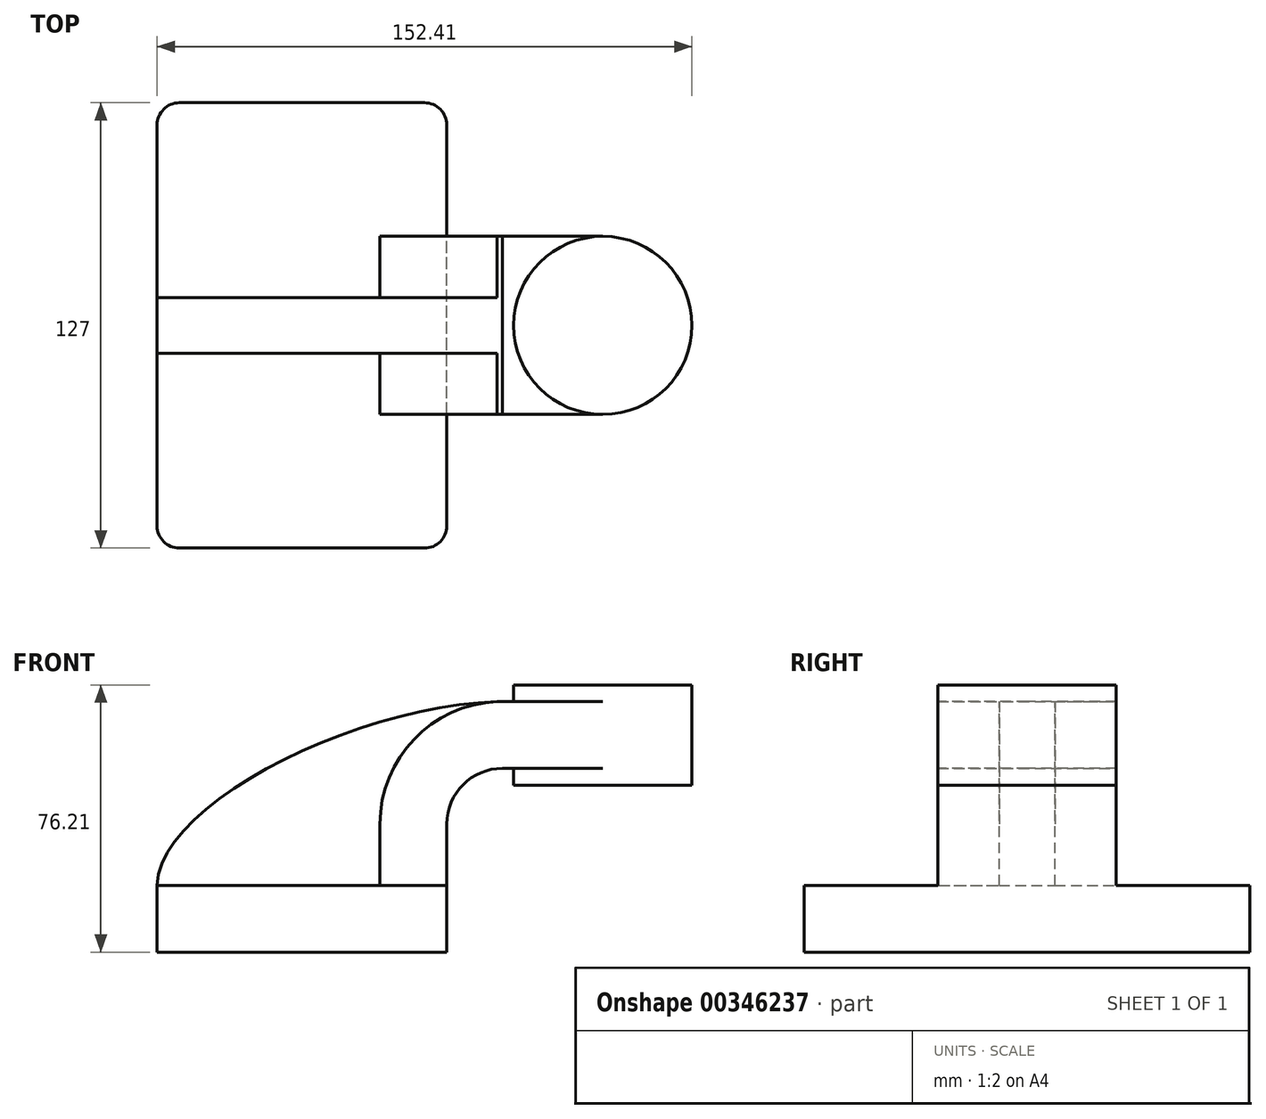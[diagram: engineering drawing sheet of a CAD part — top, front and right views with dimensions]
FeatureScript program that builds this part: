
annotation { "Feature Type Name" : "Feature", "Feature Type Description" : "" }
export const myFeature = defineFeature(function(context is Context, id is Id, definition is map)
    precondition{}
    {
        {
            var Q0;
            Q0=qCreatedBy(makeId("Front.planeOp"),FACE);
            var sketch = newSketch(context, id + "F0", { "sketchPlane" : qUnion([Q0])});
            skLineSegment(sketch, "E0.bottom", {"start": v(-41.28, -9.53) * mm, "end": v(41.28, -9.53) * mm});
            skLineSegment(sketch, "E0.top", {"start": v(-41.28, 9.52) * mm, "end": v(41.28, 9.52) * mm});
            skLineSegment(sketch, "E0.left", {"start": v(-41.28, -9.53) * mm, "end": v(-41.28, 9.52) * mm});
            skLineSegment(sketch, "E0.right", {"start": v(41.28, -9.53) * mm, "end": v(41.28, 9.52) * mm});
            skPoint(sketch, "E0.middle", {"position": v(0, 0) * mm});
            skLineSegment(sketch, "E1.bottom", {"start": v(60.32, 38.1) * mm, "end": v(111.12, 38.1) * mm});
            skLineSegment(sketch, "E1.top", {"start": v(60.32, 66.67) * mm, "end": v(111.12, 66.67) * mm});
            skLineSegment(sketch, "E1.left", {"start": v(60.32, 38.1) * mm, "end": v(60.32, 66.67) * mm});
            skLineSegment(sketch, "E1.right", {"start": v(111.12, 38.1) * mm, "end": v(111.12, 66.67) * mm});
            skPoint(sketch, "E1.middle", {"position": v(85.72, 52.39) * mm});
            skLineSegment(sketch, "E2", {"start": v(41.28, 9.52) * mm, "end": v(41.28, 27) * mm});
            skArc(sketch, "E3", {"start": v(41.27, 27) * mm, "mid": v(45.92, 38.23) * mm, "end": v(57.15, 42.88) * mm});
            skLineSegment(sketch, "E4", {"start": v(57.15, 42.88) * mm, "end": v(85.72, 42.88) * mm});
            skPoint(sketch, "E4.endSnap0", {"position": v(85.72, 38.1) * mm});
            skLineSegment(sketch, "E5.0", {"start": v(57.15, 61.93) * mm, "end": v(85.72, 61.93) * mm});
            skArc(sketch, "E5.1", {"start": v(22.23, 27) * mm, "mid": v(32.45, 51.7) * mm, "end": v(57.15, 61.93) * mm});
            skLineSegment(sketch, "E5.2", {"start": v(22.23, 9.52) * mm, "end": v(22.23, 27) * mm});
            skLineSegment(sketch, "E6", {"start": v(85.72, 38.1) * mm, "end": v(85.72, 66.67) * mm});
            skFitSpline(sketch, "E7", {"points": [v(-41.28, 9.52) * mm, v(57.15, 61.93) * mm], "startDerivative": vector(1.94, 71.16) * mm, "endDerivative": vector(121.36, 1.65) * mm});
            skSolve(sketch);
        }
        {
            var Q0;
            Q0=makeQuery(id+"F0.imprint","IMPRINT",FACE,{"disambiguationData":[TD([[makeQuery(id+"F0.imprint","IMPRINT",EDGE,{"derivedFrom":sQuery(id+"F0.wireOp",EDGE,"E0.bottom")}),1.0]])]});
            extrude(context, id + "F1", {"entities" : qUnion([Q0]), "endBound" : BoundingType.SYMMETRIC, "depth" : 127 * mm});
        }
        {
            var Q0;
            {var subQ1=sQuery(id+"F0.wireOp",EDGE,"E2");Q0=makeQuery(id+"F0.imprint","IMPRINT",FACE,{"disambiguationData":[TD([[makeQuery(id+"F0.imprint","IMPRINT",EDGE,{"derivedFrom":subQ1}),1.0]])]});}
            var Q1;
            {var subQ0=sQuery(id+"F0.wireOp",EDGE,"E4");var subQ1=sQuery(id+"F0.wireOp",EDGE,"E1.left");var subQ2=makeQuery(id+"F0.imprint","INTERSECT",VERTEX,{"derivedFrom":[subQ1,subQ0]});Q1=makeQuery(id+"F0.imprint","IMPRINT",FACE,{"disambiguationData":[TD([[makeQuery(id+"F0.imprint","IMPRINT",EDGE,{"disambiguationData":[TD([[subQ2,-1.0]])],"derivedFrom":subQ1}),-1.0]])]});}
            extrude(context, id + "F2", {"entities" : qUnion([Q0, Q1]), "operationType" : NewBodyOperationType.ADD, "endBound" : BoundingType.SYMMETRIC, "depth" : 50.8 * mm});
        }
        {
            var Q0;
            {var subQ3=sQuery(id+"F0.wireOp",EDGE,"E5.2");Q0=makeQuery(id+"F0.imprint","IMPRINT",FACE,{"disambiguationData":[TD([[makeQuery(id+"F0.imprint","IMPRINT",EDGE,{"derivedFrom":subQ3}),1.0]])]});}
            extrude(context, id + "F3", {"entities" : qUnion([Q0]), "operationType" : NewBodyOperationType.ADD, "endBound" : BoundingType.SYMMETRIC, "depth" : 15.88 * mm});
        }
        {
            var Q0;
            {var subQ4=sQuery(id+"F0.wireOp",EDGE,"E1.right");Q0=makeQuery(id+"F0.imprint","IMPRINT",FACE,{"disambiguationData":[TD([[makeQuery(id+"F0.imprint","IMPRINT",EDGE,{"derivedFrom":subQ4}),1.0]])]});}
            var Q1;
            Q1=sQuery(id+"F0.wireOp",EDGE,"E6");
            revolve(context, id + "F4", {"operationType" : NewBodyOperationType.ADD, "entities" : qUnion([Q0]), "axis" : qUnion([Q1]), "revolveType" : RevolveType.FULL});
        }
        {
            var Q0;
            Q0=makeQuery(id+"F1.opExtrude","CAP_EDGE",EDGE,{"disambiguationData":[OSD([sQuery(id+"F0.wireOp",EDGE,"E0.right")])],"isStart":false});
            var Q1;
            Q1=makeQuery(id+"F1.opExtrude","CAP_EDGE",EDGE,{"disambiguationData":[OSD([sQuery(id+"F0.wireOp",EDGE,"E0.left")])],"isStart":false});
            var Q2;
            Q2=makeQuery(id+"F1.opExtrude","CAP_EDGE",EDGE,{"disambiguationData":[OSD([sQuery(id+"F0.wireOp",EDGE,"E0.right")])],"isStart":true});
            var Q3;
            Q3=makeQuery(id+"F1.opExtrude","CAP_EDGE",EDGE,{"disambiguationData":[OSD([sQuery(id+"F0.wireOp",EDGE,"E0.left")])],"isStart":true});
            fillet(context, id + "F5", {"entities" : qUnion([Q0, Q1, Q2, Q3]), "radius" : 6.35 * mm, "tangentPropagation" : true, "allowEdgeOverflow" : false});
        }
    });
